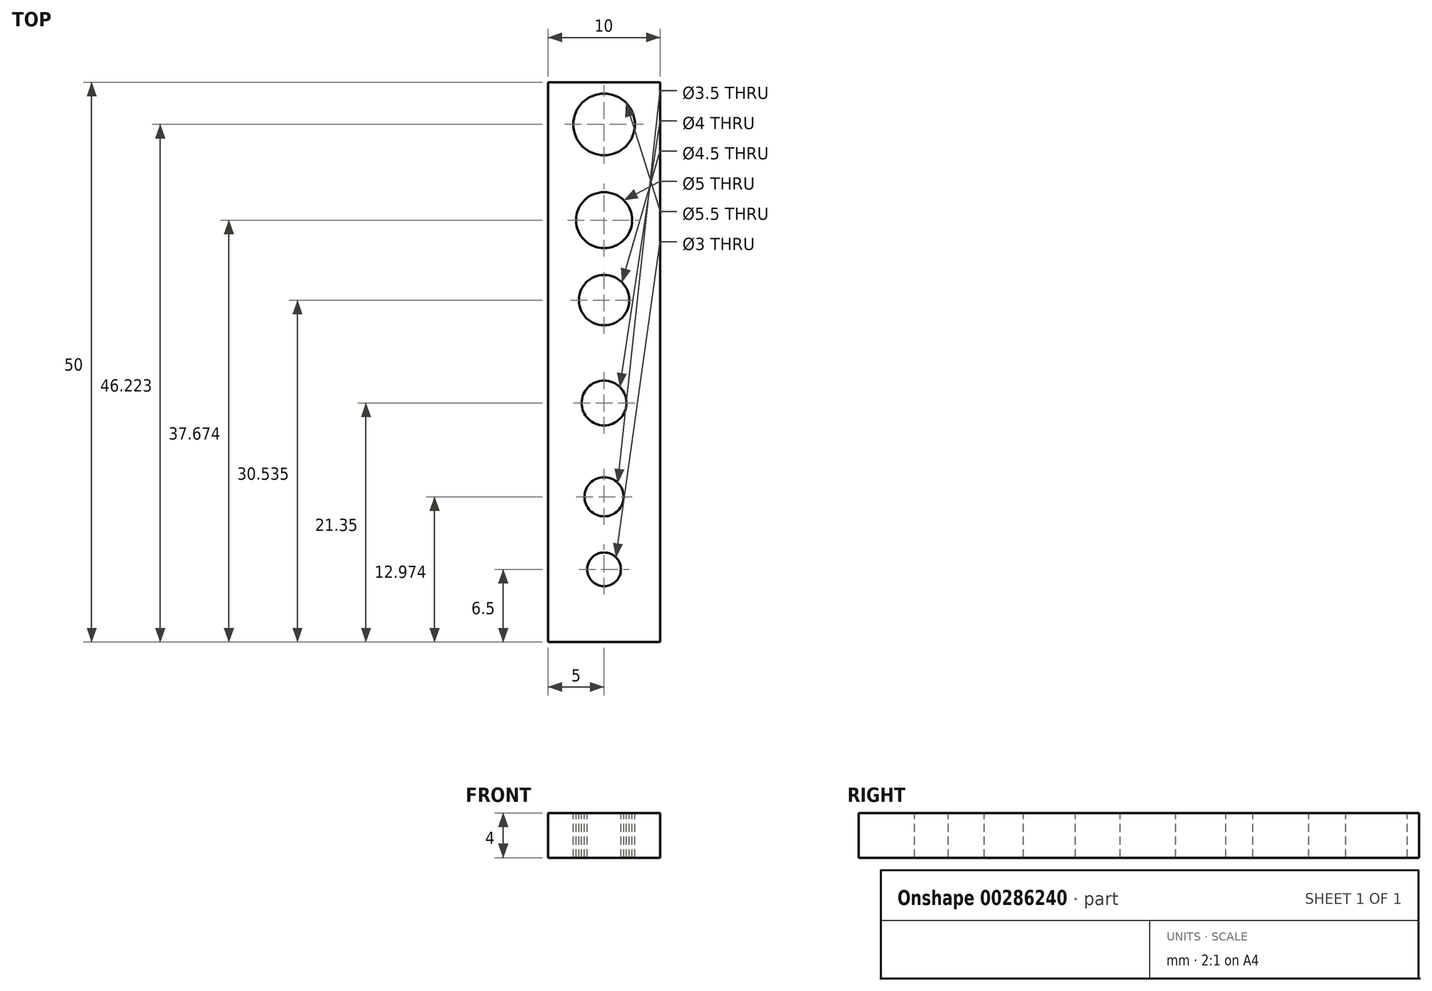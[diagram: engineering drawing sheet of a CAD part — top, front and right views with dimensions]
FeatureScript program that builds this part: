
annotation { "Feature Type Name" : "Feature", "Feature Type Description" : "" }
export const myFeature = defineFeature(function(context is Context, id is Id, definition is map)
    precondition{}
    {
        {
            var Q0;
            Q0=qCreatedBy(makeId("Top.planeOp"),FACE);
            var sketch = newSketch(context, id + "F0", { "sketchPlane" : qUnion([Q0])});
            skLineSegment(sketch, "E0.bottom", {"start": v(0, 0) * mm, "end": v(10, 0) * mm});
            skLineSegment(sketch, "E0.top", {"start": v(0, 50) * mm, "end": v(10, 50) * mm});
            skLineSegment(sketch, "E0.left", {"start": v(0, 0) * mm, "end": v(0, 50) * mm});
            skLineSegment(sketch, "E0.right", {"start": v(10, 0) * mm, "end": v(10, 50) * mm});
            skSolve(sketch);
        }
        {
            var Q0;
            Q0 = qSketchRegion(id + "F0", true);
            extrude(context, id + "F1", {"entities" : qUnion([Q0]), "depth" : 4 * mm});
        }
        {
            var Q0;
            Q0=makeQuery(id+"F1.opExtrude","CAP_FACE",FACE,{"disambiguationData":[OSD([sQuery(id+"F0.wireOp",EDGE,"E0.bottom"),sQuery(id+"F0.wireOp",EDGE,"E0.top"),sQuery(id+"F0.wireOp",EDGE,"E0.left"),sQuery(id+"F0.wireOp",EDGE,"E0.right")])],"isStart":false});
            var sketch = newSketch(context, id + "F2", { "sketchPlane" : qUnion([Q0])});
            skCircle(sketch, "E1", {"center": v(5, 6.5) * mm, "radius": 1.5 * mm});
            skLineSegment(sketch, "E2", {"start": v(5, 50) * mm, "end": v(5, 0) * mm});
            skCircle(sketch, "E3", {"center": v(5, 12.97) * mm, "radius": 1.75 * mm});
            skCircle(sketch, "E4", {"center": v(5, 21.35) * mm, "radius": 2 * mm});
            skCircle(sketch, "E5", {"center": v(5, 30.53) * mm, "radius": 2.25 * mm});
            skCircle(sketch, "E6", {"center": v(5, 37.67) * mm, "radius": 2.5 * mm});
            skCircle(sketch, "E7", {"center": v(5, 46.22) * mm, "radius": 2.75 * mm});
            skSolve(sketch);
        }
        {
            var Q0;
            Q0 = qSketchRegion(id + "F2", true);
            extrude(context, id + "F3", {"entities" : qUnion([Q0]), "operationType" : NewBodyOperationType.REMOVE, "endBound" : BoundingType.THROUGH_ALL, "oppositeDirection" : true, "depth" : 25 * mm});
        }
    });
